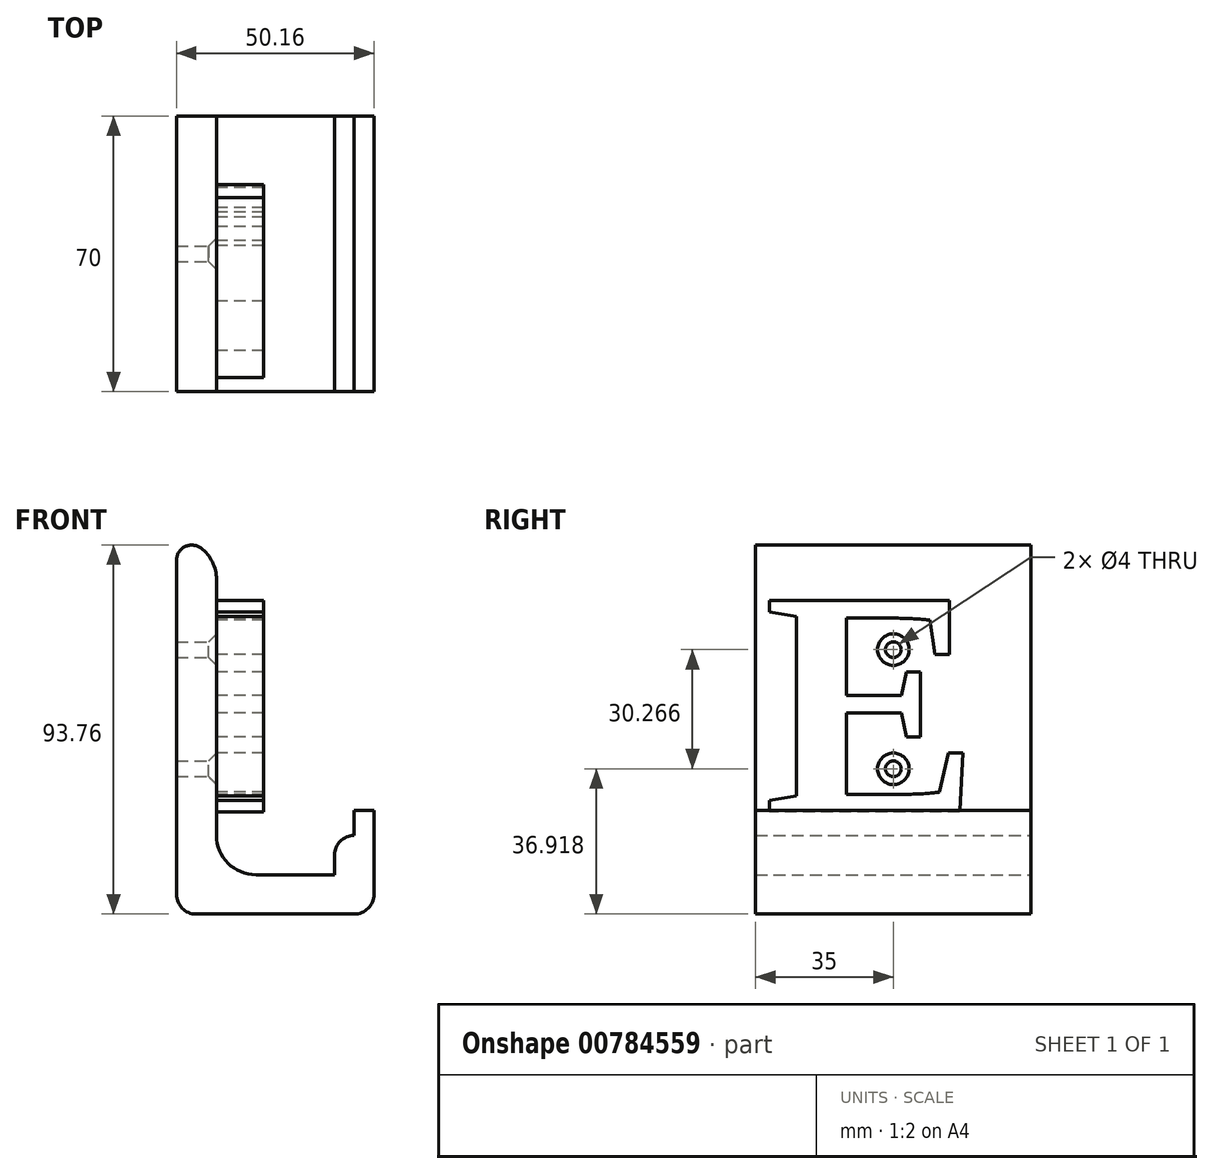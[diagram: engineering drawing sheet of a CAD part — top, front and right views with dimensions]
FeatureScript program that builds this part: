
annotation { "Feature Type Name" : "Feature", "Feature Type Description" : "" }
export const myFeature = defineFeature(function(context is Context, id is Id, definition is map)
    precondition{}
    {
        {
            var Q0;
            Q0=qCreatedBy(makeId("Front.planeOp"),FACE);
            var sketch = newSketch(context, id + "F0", { "sketchPlane" : qUnion([Q0])});
            skLineSegment(sketch, "E0", {"start": v(-20.43, 64.41) * mm, "end": v(-20.43, -20.98) * mm});
            skLineSegment(sketch, "E1", {"start": v(-15.43, -25.98) * mm, "end": v(24.73, -25.98) * mm});
            skLineSegment(sketch, "E2", {"start": v(29.73, -20.98) * mm, "end": v(29.73, -5.98) * mm});
            skLineSegment(sketch, "E3", {"start": v(29.73, -5.98) * mm, "end": v(24.73, -5.98) * mm});
            skLineSegment(sketch, "E4", {"start": v(19.73, -10.98) * mm, "end": v(19.73, -15.98) * mm});
            skLineSegment(sketch, "E5", {"start": v(19.73, -15.98) * mm, "end": v(-0.27, -15.98) * mm});
            skLineSegment(sketch, "E6", {"start": v(-10.27, -5.98) * mm, "end": v(-10.27, 59.02) * mm});
            skLineSegment(sketch, "E7", {"start": v(-20.27, 69.02) * mm, "end": v(-20.43, 69.02) * mm});
            skLineSegment(sketch, "E8", {"start": v(-20.43, 69.02) * mm, "end": v(-20.43, 64.41) * mm});
            skPoint(sketch, "E9.visualSharp", {"position": v(-10.27, 69.02) * mm});
            skArc(sketch, "E9.filletArc", {"start": v(-10.27, 59.02) * mm, "mid": v(-13.2, 66.09) * mm, "end": v(-20.27, 69.02) * mm});
            skPoint(sketch, "E10.visualSharp", {"position": v(-10.27, -15.98) * mm});
            skArc(sketch, "E10.filletArc", {"start": v(-10.27, -5.98) * mm, "mid": v(-7.34, -13.05) * mm, "end": v(-0.27, -15.98) * mm});
            skPoint(sketch, "E11.visualSharp", {"position": v(-20.43, -25.98) * mm});
            skArc(sketch, "E11.filletArc", {"start": v(-20.43, -20.98) * mm, "mid": v(-18.96, -24.52) * mm, "end": v(-15.43, -25.98) * mm});
            skPoint(sketch, "E12.visualSharp", {"position": v(19.73, -5.98) * mm});
            skArc(sketch, "E12.filletArc", {"start": v(24.73, -5.98) * mm, "mid": v(21.2, -7.45) * mm, "end": v(19.73, -10.98) * mm});
            skPoint(sketch, "E13.visualSharp", {"position": v(29.73, -25.98) * mm});
            skArc(sketch, "E13.filletArc", {"start": v(24.73, -25.98) * mm, "mid": v(28.27, -24.52) * mm, "end": v(29.73, -20.98) * mm});
            skSolve(sketch);
        }
        {
            var Q0;
            Q0=makeQuery(id+"F0.imprint","IMPRINT",FACE,{"disambiguationData":[TD([[makeQuery(id+"F0.imprint","IMPRINT",EDGE,{"derivedFrom":sQuery(id+"F0.wireOp",EDGE,"E0")}),1.0]])]});
            extrude(context, id + "F1", {"entities" : qUnion([Q0]), "endBound" : BoundingType.SYMMETRIC, "depth" : 70 * mm, "offsetDistance" : 25 * mm});
        }
        {
            var Q0;
            Q0=makeQuery(id+"F1.opExtrude","SWEPT_FACE",FACE,{"disambiguationData":[OSD([sQuery(id+"F0.wireOp",EDGE,"E6")])]});
            var sketch = newSketch(context, id + "F2", { "sketchPlane" : qUnion([Q0])});
            skText(sketch, "E14", { "text": "E", "fontName": "Tinos-Bold.ttf"});
            const initialGuessF2  = {"E14": [-0.03284, 0, 1, 0, 0.059]};
            skSetInitialGuess(sketch, initialGuessF2);
            skSolve(sketch);
        }
        {
            var Q0;
            Q0 = qSketchRegion(id + "F2", true);
            extrude(context, id + "F3", {"entities" : qUnion([Q0]), "operationType" : NewBodyOperationType.ADD, "depth" : 12 * mm, "offsetDistance" : 25 * mm});
        }
        {
            var Q0;
            Q0=makeQuery(id+"F1.opExtrude","SWEPT_FACE",FACE,{"disambiguationData":[OSD([sQuery(id+"F0.wireOp",EDGE,"E6")])]});
            var sketch = newSketch(context, id + "F4", { "sketchPlane" : qUnion([Q0])});
            skPoint(sketch, "E15", {"position": v(0, 41.2) * mm});
            skPoint(sketch, "E16", {"position": v(0, 10.94) * mm});
            skSolve(sketch);
        }
        {
            var Q0;
            Q0=sQuery(id+"F4.wireOp",VERTEX,"E15");
            var Q1;
            Q1=makeQuery(id+"F1.opExtrude","SWEPT_BODY",BODY,{"disambiguationData":[OSD([sQuery(id+"F0.wireOp",EDGE,"E0"),sQuery(id+"F0.wireOp",EDGE,"E1"),sQuery(id+"F0.wireOp",EDGE,"E2"),sQuery(id+"F0.wireOp",EDGE,"E3"),sQuery(id+"F0.wireOp",EDGE,"E4"),sQuery(id+"F0.wireOp",EDGE,"E5"),sQuery(id+"F0.wireOp",EDGE,"E6"),sQuery(id+"F0.wireOp",EDGE,"E7"),sQuery(id+"F0.wireOp",EDGE,"E8"),sQuery(id+"F0.wireOp",EDGE,"E9.filletArc"),sQuery(id+"F0.wireOp",EDGE,"E10.filletArc"),sQuery(id+"F0.wireOp",EDGE,"E11.filletArc"),sQuery(id+"F0.wireOp",EDGE,"E12.filletArc"),sQuery(id+"F0.wireOp",EDGE,"E13.filletArc")])]});
            hole(context, id + "F5", {"style" : HoleStyle.C_SINK, "endStyle" : HoleEndStyle.THROUGH, "holeDiameter" : 4 * mm, "cSinkDiameter" : 8 * mm, "cSinkAngle" : 90 * degree, "majorDiameter" : 5 * mm, "isTappedThrough" : true, "tappedDepth" : 12 * mm, "tapClearance" : 3, "startFromSketch" : true, "locations" : qUnion([Q0]), "scope" : qUnion([Q1])});
        }
        {
            var Q0;
            Q0=sQuery(id+"F4.wireOp",VERTEX,"E16");
            var Q1;
            Q1=makeQuery(id+"F1.opExtrude","SWEPT_BODY",BODY,{"disambiguationData":[OSD([sQuery(id+"F0.wireOp",EDGE,"E0"),sQuery(id+"F0.wireOp",EDGE,"E1"),sQuery(id+"F0.wireOp",EDGE,"E2"),sQuery(id+"F0.wireOp",EDGE,"E3"),sQuery(id+"F0.wireOp",EDGE,"E4"),sQuery(id+"F0.wireOp",EDGE,"E5"),sQuery(id+"F0.wireOp",EDGE,"E6"),sQuery(id+"F0.wireOp",EDGE,"E7"),sQuery(id+"F0.wireOp",EDGE,"E8"),sQuery(id+"F0.wireOp",EDGE,"E9.filletArc"),sQuery(id+"F0.wireOp",EDGE,"E10.filletArc"),sQuery(id+"F0.wireOp",EDGE,"E11.filletArc"),sQuery(id+"F0.wireOp",EDGE,"E12.filletArc"),sQuery(id+"F0.wireOp",EDGE,"E13.filletArc")])]});
            hole(context, id + "F6", {"style" : HoleStyle.C_SINK, "endStyle" : HoleEndStyle.THROUGH, "holeDiameter" : 4 * mm, "cSinkDiameter" : 8 * mm, "cSinkAngle" : 90 * degree, "majorDiameter" : 5 * mm, "isTappedThrough" : true, "tappedDepth" : 12 * mm, "tapClearance" : 3, "startFromSketch" : true, "locations" : qUnion([Q0]), "scope" : qUnion([Q1])});
        }
        {
            var Q0;
            Q0=makeQuery(id+"F1.opExtrude","SWEPT_FACE",FACE,{"disambiguationData":[OSD([sQuery(id+"F0.wireOp",EDGE,"E3")])]});
            extrude(context, id + "F7", {"entities" : qUnion([Q0]), "operationType" : NewBodyOperationType.ADD, "depth" : 6.3 * mm, "offsetDistance" : 25 * mm});
        }
        {
            var Q0;
            Q0=makeQuery(id+"F1.opExtrude","SWEPT_EDGE",EDGE,{"disambiguationData":[OSD([sQuery(id+"F0.wireOp",EDGE,"E7"),sQuery(id+"F0.wireOp",EDGE,"E8")])]});
            fillet(context, id + "F8", {"entities" : qUnion([Q0]), "radius" : 3.86 * mm, "tangentPropagation" : true, "allowEdgeOverflow" : false});
        }
    });
